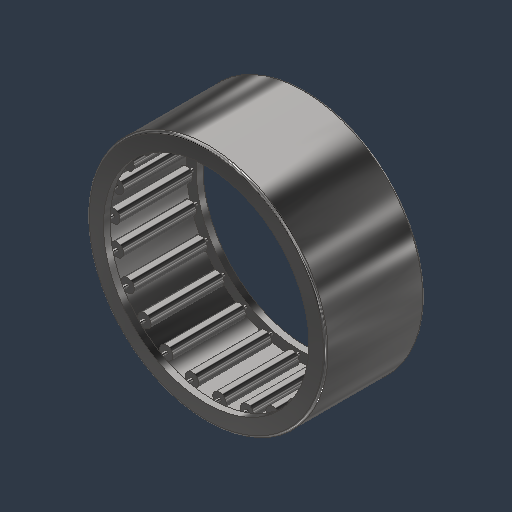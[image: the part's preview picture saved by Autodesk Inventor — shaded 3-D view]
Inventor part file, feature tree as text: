
AUTODESK INVENTOR PART (.ipt)
format: ipt  version: 2024.3 (Build 283343000, 343)  size: 303,104 bytes
history: native  units: mm (DEFAULTED — no unit token found)
features: other x46, revolve x2, fillet x1
ambient origin geometry x8: Origin, YZ Plane, XZ Plane, XY Plane, X Axis, Y Axis, Z Axis, Center Point
bodies: Solid1 (feature_tree), Solid2 (feature_tree), Solid3 (feature_tree), Solid4 (feature_tree), Solid5 (feature_tree), Solid6 (feature_tree), Solid7 (feature_tree), Solid8 (feature_tree), Solid9 (feature_tree), Solid10 (feature_tree), Solid11 (feature_tree), Solid12 (feature_tree), Solid13 (feature_tree), Solid14 (feature_tree), Solid15 (feature_tree), Solid16 (feature_tree), Solid17 (feature_tree), Solid18 (feature_tree), Solid19 (feature_tree), Solid20 (feature_tree), Solid21 (feature_tree), Solid22 (feature_tree), Solid23 (feature_tree), Solid24 (feature_tree), Solid25 (feature_tree), Solid26 (feature_tree), Solid27 (feature_tree), Solid28 (feature_tree), Solid29 (feature_tree), Solid30 (feature_tree), Solid31 (feature_tree), Solid32 (feature_tree), Solid33 (feature_tree), Solid34 (feature_tree), Solid35 (feature_tree), Solid36 (feature_tree), Solid37 (feature_tree), Solid38 (feature_tree), Solid39 (feature_tree), Solid40 (feature_tree), Solid41 (feature_tree), Solid42 (feature_tree), Solid43 (feature_tree), Solid44 (feature_tree), Solid45 (feature_tree), Solid46 (feature_tree), Solid47 (feature_tree), Solid48 (feature_tree), Solid49 (feature_tree)
feature tree (49):
  fillet  "Fillet1"  [1 undecoded]
  revolve  "Revolve2"  [1 undecoded]
  revolve  "Revolve3"  [1 undecoded]
  other  "CirPattern1[1]"
  other  "CirPattern1[2]"
  other  "CirPattern1[3]"
  other  "CirPattern1[4]"
  other  "CirPattern1[5]"
  other  "CirPattern1[6]"
  other  "CirPattern1[7]"
  other  "CirPattern1[8]"
  other  "CirPattern1[9]"
  other  "CirPattern1[10]"
  other  "CirPattern1[11]"
  other  "CirPattern1[12]"
  other  "CirPattern1[13]"
  other  "CirPattern1[14]"
  other  "CirPattern1[15]"
  other  "CirPattern1[16]"
  other  "CirPattern1[17]"
  other  "CirPattern1[18]"
  other  "CirPattern1[19]"
  other  "CirPattern1[20]"
  other  "CirPattern1[21]"
  other  "CirPattern1[22]"
  other  "CirPattern1[23]"
  other  "CirPattern1[24]"
  other  "CirPattern1[25]"
  other  "CirPattern1[26]"
  other  "CirPattern1[27]"
  other  "CirPattern1[28]"
  other  "CirPattern1[29]"
  other  "CirPattern1[30]"
  other  "CirPattern1[31]"
  other  "CirPattern1[32]"
  other  "CirPattern1[33]"
  other  "CirPattern1[34]"
  other  "CirPattern1[35]"
  other  "CirPattern1[36]"
  other  "CirPattern1[37]"
  other  "CirPattern1[38]"
  other  "CirPattern1[39]"
  other  "CirPattern1[40]"
  other  "CirPattern1[41]"
  other  "CirPattern1[42]"
  other  "CirPattern1[43]"
  other  "CirPattern1[44]"
  other  "CirPattern1[45]"
  other  "CirPattern1[46]"
note: 3 required parameter values undecoded (feature->parameter linkage not recoverable at this tier; creation-order binding heuristic only, values carry confidence <= 0.55)
